# Revit family: FT6QLIC
name_source: partatom
category: Lighting Fixtures
revit_build: Autodesk Revit 2014 (Build: 20130308_1515(x64)
units: mm (PartAtom-declared; Revit-internal decimal feet)

## types (4) — shared parameters
Apparent Load = 0 VA
Color Filter = 16777215
Default Elevation = 48.000"
Description = 6in Fire Resistant, AirShield LED Recessed Downlight IC Rated 120V
Dimming Lamp Color Temperature Shift = <None>
Emit Shape Visible in Rendering = No
Emit from Circle Diameter = 6.000"
Glass = Glass - Finish
Manufacturer = Prescolite
Model = FT6QLIC
Photometric Web File = 6184.ies
Product Documentation Link = https://hubbellcdn.com
Product Page URL = https://www.hubbell.com
Tilt Angle = -90.00°
URL = https://www.hubbell.com
Voltage = 120 V
Wattage Comments = 12W- 14W

## per-type parameters (varying)
| type | Hardware Finish | Lamp |
| FT6QLIC-WH | White |  |
| FT6QLIC-BL | Black |  |
| FT6QLIC-BA | Brushed Aluminum |  |
| FT6QLIC-BZ | Bronze | LED |

## geometry (parser evidence)
native form markers: Blend x4, Sweep x4
no freeform markers — native parametric forms only
